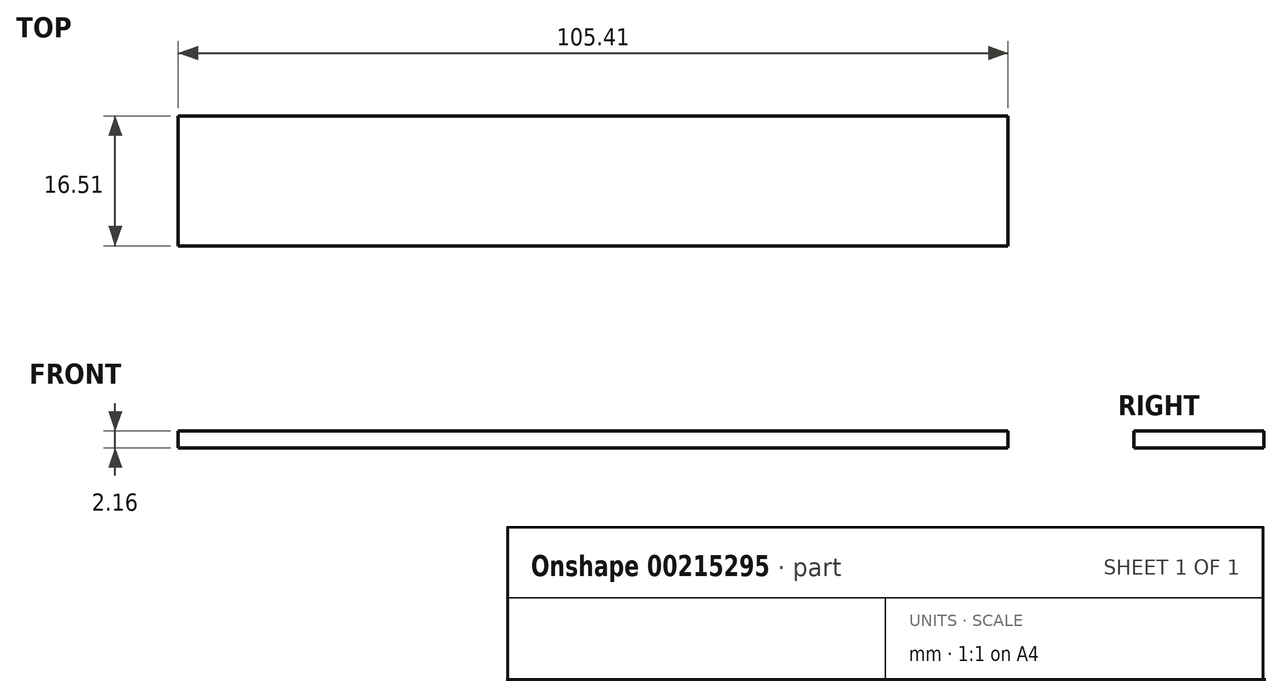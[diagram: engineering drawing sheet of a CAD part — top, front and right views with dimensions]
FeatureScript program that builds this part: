
annotation { "Feature Type Name" : "Feature", "Feature Type Description" : "" }
export const myFeature = defineFeature(function(context is Context, id is Id, definition is map)
    precondition{}
    {
        {
            var Q0;
            Q0=qCreatedBy(makeId("Top.planeOp"),FACE);
            var sketch = newSketch(context, id + "F0", { "sketchPlane" : qUnion([Q0])});
            skLineSegment(sketch, "E0.bottom", {"start": v(0, 0) * mm, "end": v(105.4, 0) * mm});
            skLineSegment(sketch, "E0.top", {"start": v(0, -16.5) * mm, "end": v(105.41, -16.5) * mm});
            skLineSegment(sketch, "E0.left", {"start": v(0, 0) * mm, "end": v(0, -16.5) * mm});
            skLineSegment(sketch, "E0.right", {"start": v(105.41, 0) * mm, "end": v(105.41, -16.5) * mm});
            skSolve(sketch);
        }
        {
            var Q0;
            Q0 = qSketchRegion(id + "F0", true);
            extrude(context, id + "F1", {"entities" : qUnion([Q0]), "depth" : 2.16 * mm});
        }
    });
